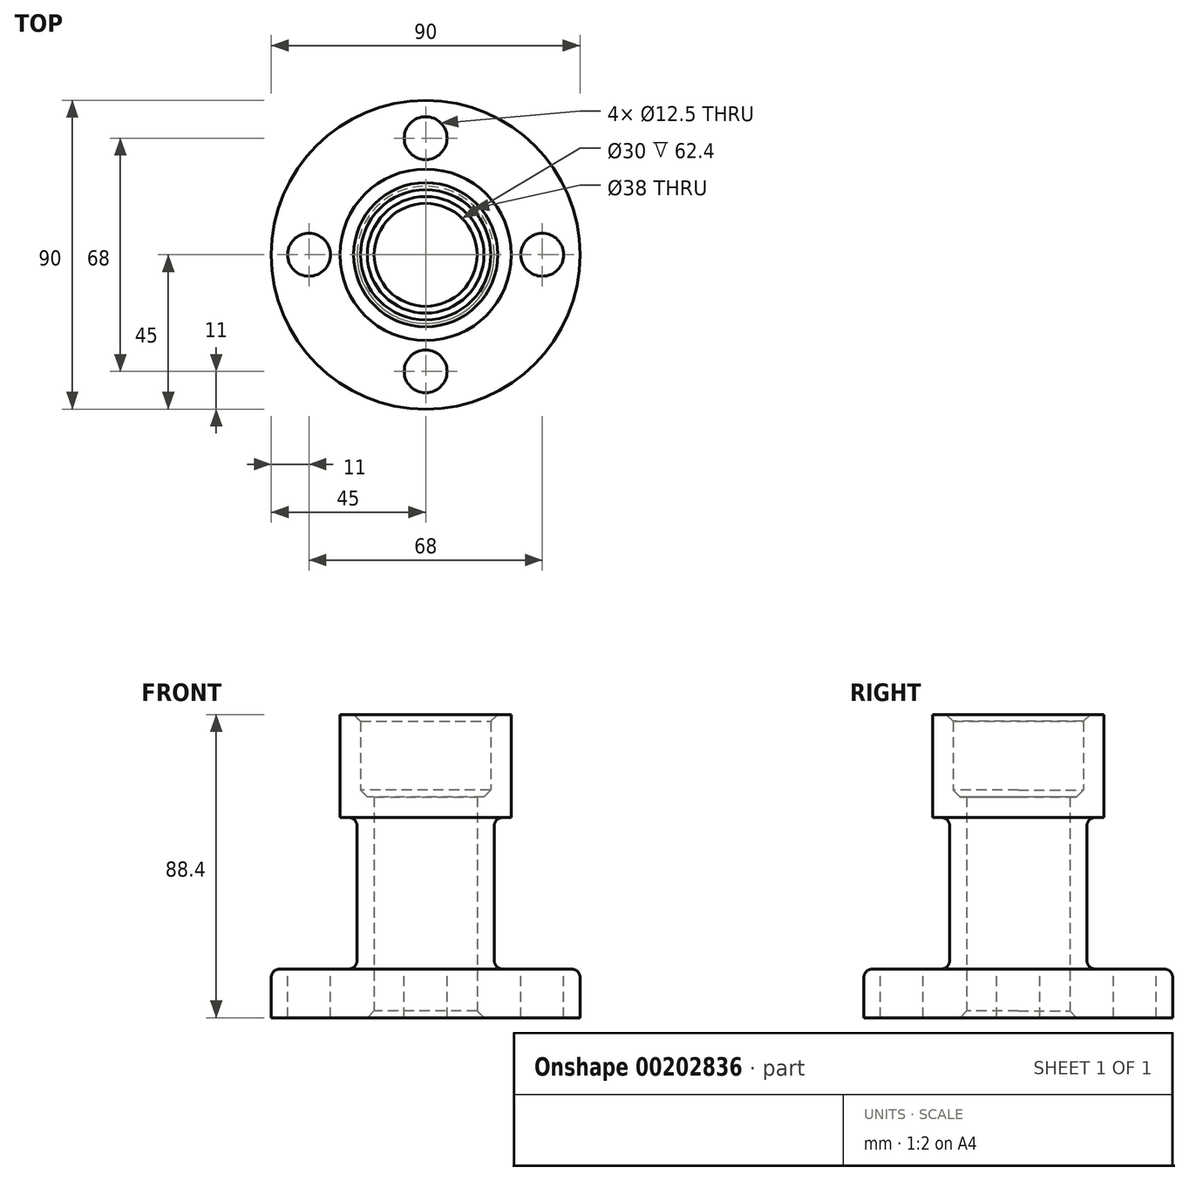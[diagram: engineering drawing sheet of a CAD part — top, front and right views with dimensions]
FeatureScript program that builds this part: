
annotation { "Feature Type Name" : "Feature", "Feature Type Description" : "" }
export const myFeature = defineFeature(function(context is Context, id is Id, definition is map)
    precondition{}
    {
        {
            var Q0;
            Q0=qCreatedBy(makeId("Front.planeOp"),FACE);
            var sketch = newSketch(context, id + "F0", { "sketchPlane" : qUnion([Q0])});
            skLineSegment(sketch, "E0", {"start": v(-20, 14.2) * mm, "end": v(-20, 58.4) * mm});
            skLineSegment(sketch, "E1", {"start": v(-45, 0) * mm, "end": v(-45, 14.2) * mm});
            skLineSegment(sketch, "E2", {"start": v(-45, 14.2) * mm, "end": v(-20, 14.2) * mm});
            skLineSegment(sketch, "E3", {"start": v(-20, 58.4) * mm, "end": v(-25, 58.4) * mm});
            skLineSegment(sketch, "E4", {"start": v(-25, 58.4) * mm, "end": v(-25, 88.4) * mm});
            skLineSegment(sketch, "E5", {"start": v(-15, 0) * mm, "end": v(-15, 64.4) * mm});
            skLineSegment(sketch, "E6", {"start": v(-45, 0) * mm, "end": v(-15, 0) * mm});
            skLineSegment(sketch, "E7", {"start": v(-19, 88.4) * mm, "end": v(-19, 64.4) * mm});
            skLineSegment(sketch, "E8", {"start": v(-19, 64.4) * mm, "end": v(-15, 64.4) * mm});
            skLineSegment(sketch, "E9", {"start": v(-19, 88.4) * mm, "end": v(-25, 88.4) * mm});
            skLineSegment(sketch, "E10", {"start": v(0, -28.51) * mm, "end": v(0, 97.7) * mm, "construction": true});
            skSolve(sketch);
        }
        {
            var Q0;
            Q0 = qSketchRegion(id + "F0", true);
            var Q1;
            Q1=sQuery(id+"F0.wireOp",EDGE,"E10");
            revolve(context, id + "F1", {"entities" : qUnion([Q0]), "axis" : qUnion([Q1]), "revolveType" : RevolveType.FULL});
        }
        {
            var Q0;
            Q0=makeQuery(id+"F1.opRevolve","SWEPT_EDGE",EDGE,{"disambiguationData":[OSD([sQuery(id+"F0.wireOp",EDGE,"E5"),sQuery(id+"F0.wireOp",EDGE,"E6")])]});
            var Q1;
            Q1=makeQuery(id+"F1.opRevolve","SWEPT_EDGE",EDGE,{"disambiguationData":[OSD([sQuery(id+"F0.wireOp",EDGE,"E7"),sQuery(id+"F0.wireOp",EDGE,"E9")])]});
            var Q2;
            Q2=makeQuery(id+"F1.opRevolve","SWEPT_EDGE",EDGE,{"disambiguationData":[OSD([sQuery(id+"F0.wireOp",EDGE,"E7"),sQuery(id+"F0.wireOp",EDGE,"E8")])]});
            chamfer(context, id + "F2", {"entities" : qUnion([Q0, Q1, Q2]), "width" : 2 * mm, "tangentPropagation" : true});
        }
        {
            var Q0;
            Q0=makeQuery(id+"F1.opRevolve","SWEPT_EDGE",EDGE,{"disambiguationData":[OSD([sQuery(id+"F0.wireOp",EDGE,"E0"),sQuery(id+"F0.wireOp",EDGE,"E2")])]});
            var Q1;
            Q1=makeQuery(id+"F1.opRevolve","SWEPT_EDGE",EDGE,{"disambiguationData":[OSD([sQuery(id+"F0.wireOp",EDGE,"E0"),sQuery(id+"F0.wireOp",EDGE,"E3")])]});
            var Q2;
            Q2=makeQuery(id+"F1.opRevolve","SWEPT_EDGE",EDGE,{"disambiguationData":[OSD([sQuery(id+"F0.wireOp",EDGE,"E1"),sQuery(id+"F0.wireOp",EDGE,"E2")])]});
            fillet(context, id + "F3", {"entities" : qUnion([Q0, Q1, Q2]), "radius" : 2.5 * mm, "tangentPropagation" : true, "allowEdgeOverflow" : false});
        }
        {
            var Q0;
            Q0=makeQuery(id+"F1.opRevolve","SWEPT_FACE",FACE,{"disambiguationData":[OSD([sQuery(id+"F0.wireOp",EDGE,"E2")])]});
            var sketch = newSketch(context, id + "F4", { "sketchPlane" : qUnion([Q0])});
            skCircle(sketch, "E11", {"center": v(0, 34) * mm, "radius": 6.25 * mm});
            skCircle(sketch, "E12.1.0", {"center": v(-34, 0) * mm, "radius": 6.25 * mm});
            skCircle(sketch, "E12.2.0", {"center": v(0, -34) * mm, "radius": 6.25 * mm});
            skCircle(sketch, "E12.3.0", {"center": v(34, 0) * mm, "radius": 6.25 * mm});
            skPoint(sketch, "E12.center", {"position": v(0, 0) * mm});
            skSolve(sketch);
        }
        {
            var Q0;
            Q0 = qSketchRegion(id + "F4", true);
            var Q1;
            Q1=makeQuery(id+"F1.opRevolve","SWEPT_FACE",FACE,{"disambiguationData":[OSD([sQuery(id+"F0.wireOp",EDGE,"E6")])]});
            extrude(context, id + "F5", {"entities" : qUnion([Q0]), "operationType" : NewBodyOperationType.REMOVE, "endBound" : BoundingType.UP_TO_SURFACE, "oppositeDirection" : true, "endBoundEntityFace" : qUnion([Q1]), "depth" : 25 * mm});
        }
    });
